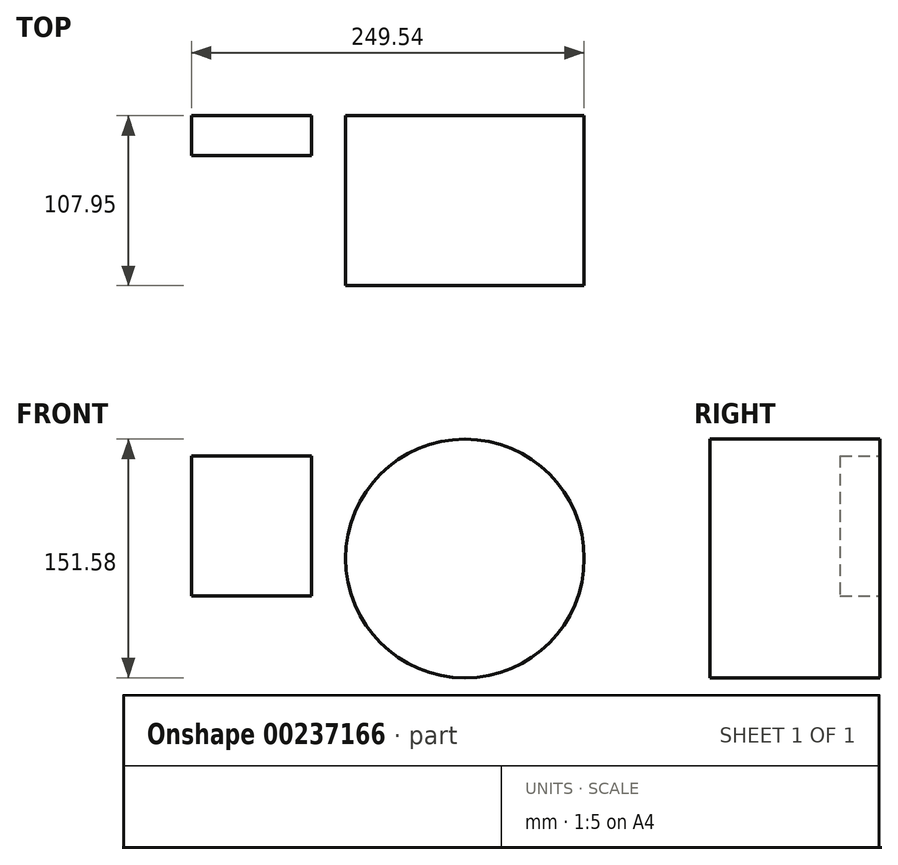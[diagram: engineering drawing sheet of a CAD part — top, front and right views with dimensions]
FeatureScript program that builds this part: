
annotation { "Feature Type Name" : "Feature", "Feature Type Description" : "" }
export const myFeature = defineFeature(function(context is Context, id is Id, definition is map)
    precondition{}
    {
        {
            var Q0;
            Q0=qCreatedBy(makeId("Front.planeOp"),FACE);
            var sketch = newSketch(context, id + "F0", { "sketchPlane" : qUnion([Q0])});
            skCircle(sketch, "E0", {"center": v(0, 0) * mm, "radius": 75.8 * mm});
            skSolve(sketch);
        }
        {
            var Q0;
            Q0 = qSketchRegion(id + "F0", true);
            extrude(context, id + "F1", {"entities" : qUnion([Q0]), "depth" : 107.95 * mm});
        }
        {
            var Q0;
            Q0=qCreatedBy(makeId("Front.planeOp"),FACE);
            var sketch = newSketch(context, id + "F2", { "sketchPlane" : qUnion([Q0])});
            skLineSegment(sketch, "E1.bottom", {"start": v(-173.75, 65.25) * mm, "end": v(-97.55, 65.25) * mm});
            skLineSegment(sketch, "E1.top", {"start": v(-173.75, -23.65) * mm, "end": v(-97.55, -23.65) * mm});
            skLineSegment(sketch, "E1.left", {"start": v(-173.75, 65.25) * mm, "end": v(-173.75, -23.65) * mm});
            skLineSegment(sketch, "E1.right", {"start": v(-97.55, 65.25) * mm, "end": v(-97.55, -23.65) * mm});
            skSolve(sketch);
        }
        {
            var Q0;
            Q0=makeQuery(id+"F2.imprint","IMPRINT",FACE,{"disambiguationData":[TD([[makeQuery(id+"F2.imprint","IMPRINT",EDGE,{"derivedFrom":sQuery(id+"F2.wireOp",EDGE,"E1.bottom")}),-1.0]])]});
            extrude(context, id + "F3", {"entities" : qUnion([Q0]), "depth" : 25.4 * mm});
        }
    });
